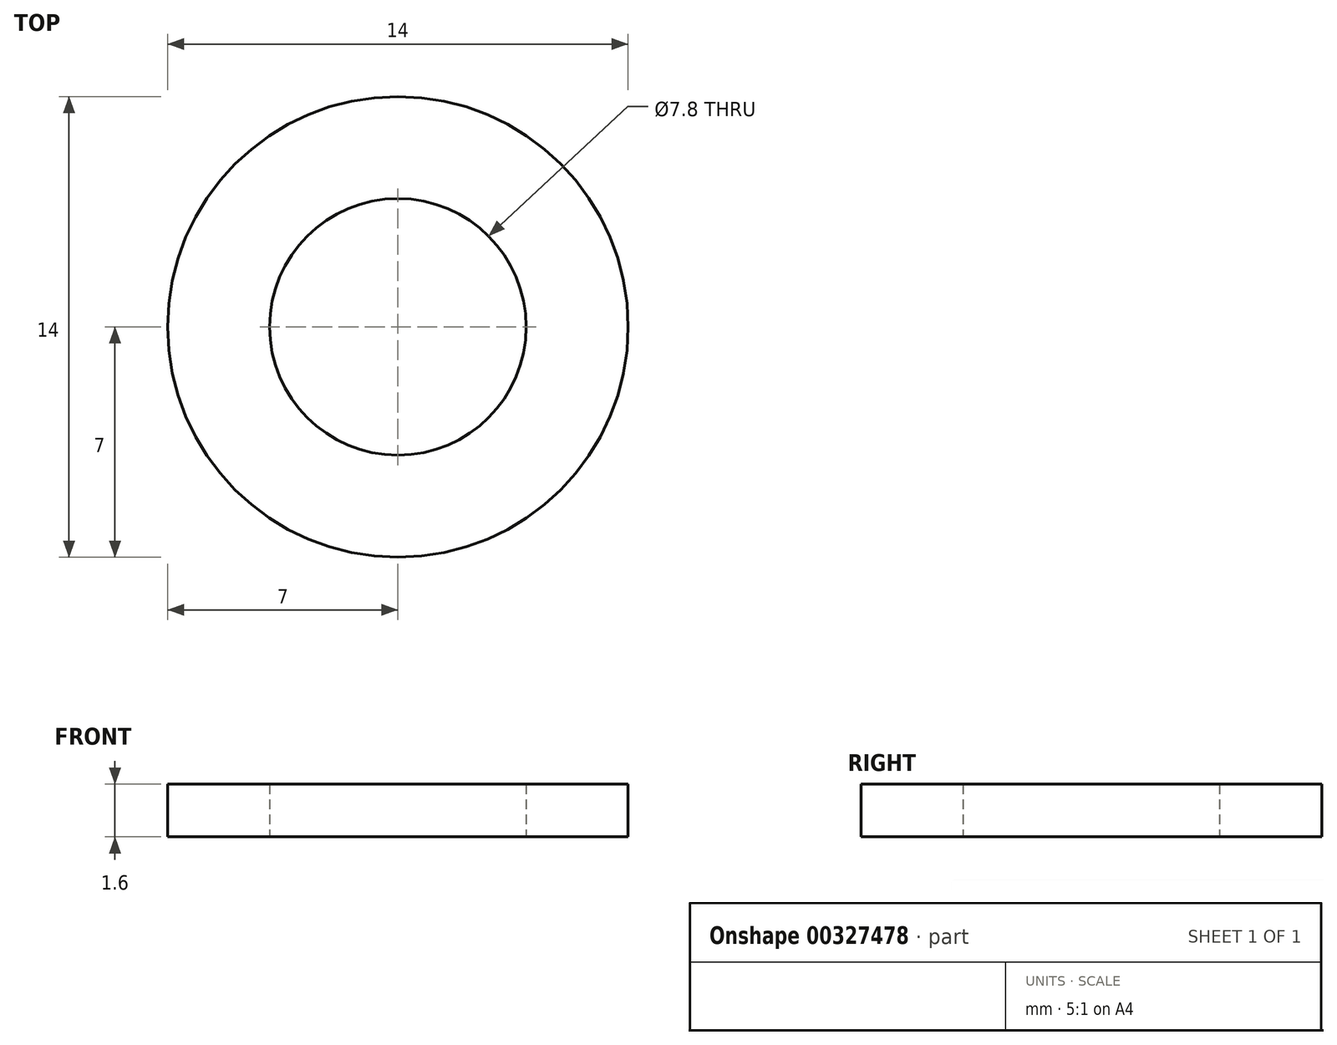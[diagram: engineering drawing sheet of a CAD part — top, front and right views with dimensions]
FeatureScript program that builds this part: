
annotation { "Feature Type Name" : "Feature", "Feature Type Description" : "" }
export const myFeature = defineFeature(function(context is Context, id is Id, definition is map)
    precondition{}
    {
        {
            var Q0;
            Q0=qCreatedBy(makeId("Top.planeOp"),FACE);
            var sketch = newSketch(context, id + "F0", { "sketchPlane" : qUnion([Q0])});
            skCircle(sketch, "E0", {"center": v(0, 0) * mm, "radius": 3.9 * mm});
            skCircle(sketch, "E1", {"center": v(0, 0) * mm, "radius": 7 * mm});
            skSolve(sketch);
        }
        {
            var Q0;
            Q0=makeQuery(id+"F0.imprint","IMPRINT",FACE,{"disambiguationData":[TD([[makeQuery(id+"F0.imprint","IMPRINT",EDGE,{"derivedFrom":sQuery(id+"F0.wireOp",EDGE,"E0")}),-1.0]])]});
            extrude(context, id + "F1", {"entities" : qUnion([Q0]), "depth" : 1.6 * mm});
        }
    });
